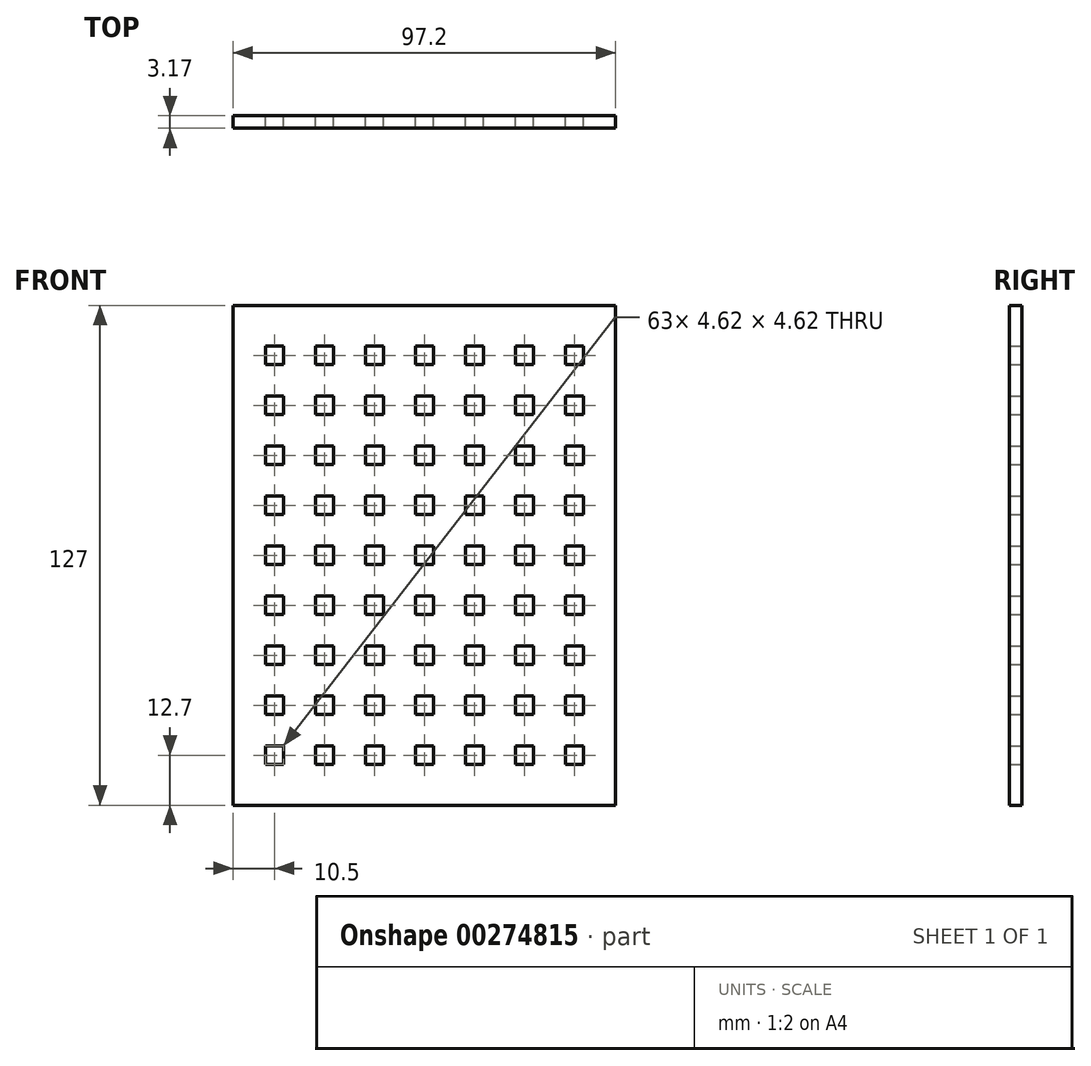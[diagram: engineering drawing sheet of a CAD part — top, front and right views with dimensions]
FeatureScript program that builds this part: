
annotation { "Feature Type Name" : "Feature", "Feature Type Description" : "" }
export const myFeature = defineFeature(function(context is Context, id is Id, definition is map)
    precondition{}
    {
        {
            var Q0;
            Q0=qCreatedBy(makeId("Front.planeOp"),FACE);
            var sketch = newSketch(context, id + "F0", { "sketchPlane" : qUnion([Q0])});
            skLineSegment(sketch, "E0.bottom", {"start": v(48.6, 63.5) * mm, "end": v(-48.6, 63.5) * mm});
            skLineSegment(sketch, "E0.top", {"start": v(48.6, -63.5) * mm, "end": v(-48.6, -63.5) * mm});
            skLineSegment(sketch, "E0.left", {"start": v(48.6, 63.5) * mm, "end": v(48.6, -63.5) * mm});
            skLineSegment(sketch, "E0.right", {"start": v(-48.6, 63.5) * mm, "end": v(-48.6, -63.5) * mm});
            skPoint(sketch, "E0.middle", {"position": v(0, 0) * mm});
            skLineSegment(sketch, "E1.bottom", {"start": v(2.31, 2.31) * mm, "end": v(-2.31, 2.31) * mm});
            skLineSegment(sketch, "E1.top", {"start": v(2.31, -2.31) * mm, "end": v(-2.31, -2.31) * mm});
            skLineSegment(sketch, "E1.left", {"start": v(2.31, 2.31) * mm, "end": v(2.31, -2.31) * mm});
            skLineSegment(sketch, "E1.right", {"start": v(-2.31, 2.31) * mm, "end": v(-2.31, -2.31) * mm});
            skLineSegment(sketch, "E2.0.1.0", {"start": v(2.31, -10.39) * mm, "end": v(-2.31, -10.39) * mm});
            skLineSegment(sketch, "E2.0.1.1", {"start": v(2.31, -15.01) * mm, "end": v(-2.31, -15.01) * mm});
            skLineSegment(sketch, "E2.0.1.2", {"start": v(2.31, -10.39) * mm, "end": v(2.31, -15.01) * mm});
            skPoint(sketch, "E2.0.1.3", {"position": v(0, -12.7) * mm});
            skLineSegment(sketch, "E2.0.1.4", {"start": v(-2.31, -10.39) * mm, "end": v(-2.31, -15.01) * mm});
            skPoint(sketch, "E2.0.1.5", {"position": v(0, -12.7) * mm});
            skLineSegment(sketch, "E2.0.2.0", {"start": v(2.31, -23.09) * mm, "end": v(-2.31, -23.09) * mm});
            skLineSegment(sketch, "E2.0.2.1", {"start": v(2.31, -27.71) * mm, "end": v(-2.31, -27.71) * mm});
            skLineSegment(sketch, "E2.0.2.2", {"start": v(2.31, -23.09) * mm, "end": v(2.31, -27.71) * mm});
            skPoint(sketch, "E2.0.2.3", {"position": v(0, -25.4) * mm});
            skLineSegment(sketch, "E2.0.2.4", {"start": v(-2.31, -23.09) * mm, "end": v(-2.31, -27.71) * mm});
            skPoint(sketch, "E2.0.2.5", {"position": v(0, -25.4) * mm});
            skLineSegment(sketch, "E2.0.3.0", {"start": v(2.31, -35.79) * mm, "end": v(-2.31, -35.79) * mm});
            skLineSegment(sketch, "E2.0.3.1", {"start": v(2.31, -40.41) * mm, "end": v(-2.31, -40.41) * mm});
            skLineSegment(sketch, "E2.0.3.2", {"start": v(2.31, -35.79) * mm, "end": v(2.31, -40.41) * mm});
            skPoint(sketch, "E2.0.3.3", {"position": v(0, -38.1) * mm});
            skLineSegment(sketch, "E2.0.3.4", {"start": v(-2.31, -35.79) * mm, "end": v(-2.31, -40.41) * mm});
            skPoint(sketch, "E2.0.3.5", {"position": v(0, -38.1) * mm});
            skLineSegment(sketch, "E2.0.4.0", {"start": v(2.31, -48.49) * mm, "end": v(-2.31, -48.49) * mm});
            skLineSegment(sketch, "E2.0.4.1", {"start": v(2.31, -53.11) * mm, "end": v(-2.31, -53.11) * mm});
            skLineSegment(sketch, "E2.0.4.2", {"start": v(2.31, -48.49) * mm, "end": v(2.31, -53.11) * mm});
            skPoint(sketch, "E2.0.4.3", {"position": v(0, -50.8) * mm});
            skLineSegment(sketch, "E2.0.4.4", {"start": v(-2.31, -48.49) * mm, "end": v(-2.31, -53.11) * mm});
            skPoint(sketch, "E2.0.4.5", {"position": v(0, -50.8) * mm});
            skLineSegment(sketch, "E2.1.0.0", {"start": v(15.01, 2.31) * mm, "end": v(10.39, 2.31) * mm});
            skLineSegment(sketch, "E2.1.0.1", {"start": v(15.01, -2.31) * mm, "end": v(10.39, -2.31) * mm});
            skLineSegment(sketch, "E2.1.0.2", {"start": v(15.01, 2.31) * mm, "end": v(15.01, -2.31) * mm});
            skPoint(sketch, "E2.1.0.3", {"position": v(12.7, 0) * mm});
            skLineSegment(sketch, "E2.1.0.4", {"start": v(10.39, 2.31) * mm, "end": v(10.39, -2.31) * mm});
            skPoint(sketch, "E2.1.0.5", {"position": v(12.7, 0) * mm});
            skLineSegment(sketch, "E2.1.1.0", {"start": v(15.01, -10.39) * mm, "end": v(10.39, -10.39) * mm});
            skLineSegment(sketch, "E2.1.1.1", {"start": v(15.01, -15.01) * mm, "end": v(10.39, -15.01) * mm});
            skLineSegment(sketch, "E2.1.1.2", {"start": v(15.01, -10.39) * mm, "end": v(15.01, -15.01) * mm});
            skPoint(sketch, "E2.1.1.3", {"position": v(12.7, -12.7) * mm});
            skLineSegment(sketch, "E2.1.1.4", {"start": v(10.39, -10.39) * mm, "end": v(10.39, -15.01) * mm});
            skPoint(sketch, "E2.1.1.5", {"position": v(12.7, -12.7) * mm});
            skLineSegment(sketch, "E2.1.2.0", {"start": v(15.01, -23.09) * mm, "end": v(10.39, -23.09) * mm});
            skLineSegment(sketch, "E2.1.2.1", {"start": v(15.01, -27.71) * mm, "end": v(10.39, -27.71) * mm});
            skLineSegment(sketch, "E2.1.2.2", {"start": v(15.01, -23.09) * mm, "end": v(15.01, -27.71) * mm});
            skPoint(sketch, "E2.1.2.3", {"position": v(12.7, -25.4) * mm});
            skLineSegment(sketch, "E2.1.2.4", {"start": v(10.39, -23.09) * mm, "end": v(10.39, -27.71) * mm});
            skPoint(sketch, "E2.1.2.5", {"position": v(12.7, -25.4) * mm});
            skLineSegment(sketch, "E2.1.3.0", {"start": v(15.01, -35.79) * mm, "end": v(10.39, -35.79) * mm});
            skLineSegment(sketch, "E2.1.3.1", {"start": v(15.01, -40.41) * mm, "end": v(10.39, -40.41) * mm});
            skLineSegment(sketch, "E2.1.3.2", {"start": v(15.01, -35.79) * mm, "end": v(15.01, -40.41) * mm});
            skPoint(sketch, "E2.1.3.3", {"position": v(12.7, -38.1) * mm});
            skLineSegment(sketch, "E2.1.3.4", {"start": v(10.39, -35.79) * mm, "end": v(10.39, -40.41) * mm});
            skPoint(sketch, "E2.1.3.5", {"position": v(12.7, -38.1) * mm});
            skLineSegment(sketch, "E2.1.4.0", {"start": v(15.01, -48.49) * mm, "end": v(10.39, -48.49) * mm});
            skLineSegment(sketch, "E2.1.4.1", {"start": v(15.01, -53.11) * mm, "end": v(10.39, -53.11) * mm});
            skLineSegment(sketch, "E2.1.4.2", {"start": v(15.01, -48.49) * mm, "end": v(15.01, -53.11) * mm});
            skPoint(sketch, "E2.1.4.3", {"position": v(12.7, -50.8) * mm});
            skLineSegment(sketch, "E2.1.4.4", {"start": v(10.39, -48.49) * mm, "end": v(10.39, -53.11) * mm});
            skPoint(sketch, "E2.1.4.5", {"position": v(12.7, -50.8) * mm});
            skLineSegment(sketch, "E2.2.0.0", {"start": v(27.71, 2.31) * mm, "end": v(23.09, 2.31) * mm});
            skLineSegment(sketch, "E2.2.0.1", {"start": v(27.71, -2.31) * mm, "end": v(23.09, -2.31) * mm});
            skLineSegment(sketch, "E2.2.0.2", {"start": v(27.71, 2.31) * mm, "end": v(27.71, -2.31) * mm});
            skPoint(sketch, "E2.2.0.3", {"position": v(25.4, 0) * mm});
            skLineSegment(sketch, "E2.2.0.4", {"start": v(23.09, 2.31) * mm, "end": v(23.09, -2.31) * mm});
            skPoint(sketch, "E2.2.0.5", {"position": v(25.4, 0) * mm});
            skLineSegment(sketch, "E2.2.1.0", {"start": v(27.71, -10.39) * mm, "end": v(23.09, -10.39) * mm});
            skLineSegment(sketch, "E2.2.1.1", {"start": v(27.71, -15.01) * mm, "end": v(23.09, -15.01) * mm});
            skLineSegment(sketch, "E2.2.1.2", {"start": v(27.71, -10.39) * mm, "end": v(27.71, -15.01) * mm});
            skPoint(sketch, "E2.2.1.3", {"position": v(25.4, -12.7) * mm});
            skLineSegment(sketch, "E2.2.1.4", {"start": v(23.09, -10.39) * mm, "end": v(23.09, -15.01) * mm});
            skPoint(sketch, "E2.2.1.5", {"position": v(25.4, -12.7) * mm});
            skLineSegment(sketch, "E2.2.2.0", {"start": v(27.71, -23.09) * mm, "end": v(23.09, -23.09) * mm});
            skLineSegment(sketch, "E2.2.2.1", {"start": v(27.71, -27.71) * mm, "end": v(23.09, -27.71) * mm});
            skLineSegment(sketch, "E2.2.2.2", {"start": v(27.71, -23.09) * mm, "end": v(27.71, -27.71) * mm});
            skPoint(sketch, "E2.2.2.3", {"position": v(25.4, -25.4) * mm});
            skLineSegment(sketch, "E2.2.2.4", {"start": v(23.09, -23.09) * mm, "end": v(23.09, -27.71) * mm});
            skPoint(sketch, "E2.2.2.5", {"position": v(25.4, -25.4) * mm});
            skLineSegment(sketch, "E2.2.3.0", {"start": v(27.71, -35.79) * mm, "end": v(23.09, -35.79) * mm});
            skLineSegment(sketch, "E2.2.3.1", {"start": v(27.71, -40.41) * mm, "end": v(23.09, -40.41) * mm});
            skLineSegment(sketch, "E2.2.3.2", {"start": v(27.71, -35.79) * mm, "end": v(27.71, -40.41) * mm});
            skPoint(sketch, "E2.2.3.3", {"position": v(25.4, -38.1) * mm});
            skLineSegment(sketch, "E2.2.3.4", {"start": v(23.09, -35.79) * mm, "end": v(23.09, -40.41) * mm});
            skPoint(sketch, "E2.2.3.5", {"position": v(25.4, -38.1) * mm});
            skLineSegment(sketch, "E2.2.4.0", {"start": v(27.71, -48.49) * mm, "end": v(23.09, -48.49) * mm});
            skLineSegment(sketch, "E2.2.4.1", {"start": v(27.71, -53.11) * mm, "end": v(23.09, -53.11) * mm});
            skLineSegment(sketch, "E2.2.4.2", {"start": v(27.71, -48.49) * mm, "end": v(27.71, -53.11) * mm});
            skPoint(sketch, "E2.2.4.3", {"position": v(25.4, -50.8) * mm});
            skLineSegment(sketch, "E2.2.4.4", {"start": v(23.09, -48.49) * mm, "end": v(23.09, -53.11) * mm});
            skPoint(sketch, "E2.2.4.5", {"position": v(25.4, -50.8) * mm});
            skLineSegment(sketch, "E2.3.0.0", {"start": v(40.41, 2.31) * mm, "end": v(35.79, 2.31) * mm});
            skLineSegment(sketch, "E2.3.0.1", {"start": v(40.41, -2.31) * mm, "end": v(35.79, -2.31) * mm});
            skLineSegment(sketch, "E2.3.0.2", {"start": v(40.41, 2.31) * mm, "end": v(40.41, -2.31) * mm});
            skPoint(sketch, "E2.3.0.3", {"position": v(38.1, 0) * mm});
            skLineSegment(sketch, "E2.3.0.4", {"start": v(35.79, 2.31) * mm, "end": v(35.79, -2.31) * mm});
            skPoint(sketch, "E2.3.0.5", {"position": v(38.1, 0) * mm});
            skLineSegment(sketch, "E2.3.1.0", {"start": v(40.41, -10.39) * mm, "end": v(35.79, -10.39) * mm});
            skLineSegment(sketch, "E2.3.1.1", {"start": v(40.41, -15.01) * mm, "end": v(35.79, -15.01) * mm});
            skLineSegment(sketch, "E2.3.1.2", {"start": v(40.41, -10.39) * mm, "end": v(40.41, -15.01) * mm});
            skPoint(sketch, "E2.3.1.3", {"position": v(38.1, -12.7) * mm});
            skLineSegment(sketch, "E2.3.1.4", {"start": v(35.79, -10.39) * mm, "end": v(35.79, -15.01) * mm});
            skPoint(sketch, "E2.3.1.5", {"position": v(38.1, -12.7) * mm});
            skLineSegment(sketch, "E2.3.2.0", {"start": v(40.41, -23.09) * mm, "end": v(35.79, -23.09) * mm});
            skLineSegment(sketch, "E2.3.2.1", {"start": v(40.41, -27.71) * mm, "end": v(35.79, -27.71) * mm});
            skLineSegment(sketch, "E2.3.2.2", {"start": v(40.41, -23.09) * mm, "end": v(40.41, -27.71) * mm});
            skPoint(sketch, "E2.3.2.3", {"position": v(38.1, -25.4) * mm});
            skLineSegment(sketch, "E2.3.2.4", {"start": v(35.79, -23.09) * mm, "end": v(35.79, -27.71) * mm});
            skPoint(sketch, "E2.3.2.5", {"position": v(38.1, -25.4) * mm});
            skLineSegment(sketch, "E2.3.3.0", {"start": v(40.41, -35.79) * mm, "end": v(35.79, -35.79) * mm});
            skLineSegment(sketch, "E2.3.3.1", {"start": v(40.41, -40.41) * mm, "end": v(35.79, -40.41) * mm});
            skLineSegment(sketch, "E2.3.3.2", {"start": v(40.41, -35.79) * mm, "end": v(40.41, -40.41) * mm});
            skPoint(sketch, "E2.3.3.3", {"position": v(38.1, -38.1) * mm});
            skLineSegment(sketch, "E2.3.3.4", {"start": v(35.79, -35.79) * mm, "end": v(35.79, -40.41) * mm});
            skPoint(sketch, "E2.3.3.5", {"position": v(38.1, -38.1) * mm});
            skLineSegment(sketch, "E2.3.4.0", {"start": v(40.41, -48.49) * mm, "end": v(35.79, -48.49) * mm});
            skLineSegment(sketch, "E2.3.4.1", {"start": v(40.41, -53.11) * mm, "end": v(35.79, -53.11) * mm});
            skLineSegment(sketch, "E2.3.4.2", {"start": v(40.41, -48.49) * mm, "end": v(40.41, -53.11) * mm});
            skPoint(sketch, "E2.3.4.3", {"position": v(38.1, -50.8) * mm});
            skLineSegment(sketch, "E2.3.4.4", {"start": v(35.79, -48.49) * mm, "end": v(35.79, -53.11) * mm});
            skPoint(sketch, "E2.3.4.5", {"position": v(38.1, -50.8) * mm});
            skLineSegment(sketch, "E3.MirrorCS", {"start": v(23.09, 10.39) * mm, "end": v(23.09, 15.01) * mm});
            skLineSegment(sketch, "E4.MirrorCS", {"start": v(23.09, 35.79) * mm, "end": v(23.09, 40.41) * mm});
            skLineSegment(sketch, "E5.MirrorCS", {"start": v(27.71, 53.11) * mm, "end": v(23.09, 53.11) * mm});
            skLineSegment(sketch, "E6.MirrorCS", {"start": v(2.31, 53.11) * mm, "end": v(-2.31, 53.11) * mm});
            skLineSegment(sketch, "E7.MirrorCS", {"start": v(27.71, 27.71) * mm, "end": v(23.09, 27.71) * mm});
            skLineSegment(sketch, "E8.MirrorCS", {"start": v(23.09, 48.49) * mm, "end": v(23.09, 53.11) * mm});
            skLineSegment(sketch, "E9.MirrorCS", {"start": v(23.09, -2.31) * mm, "end": v(23.09, 2.31) * mm});
            skLineSegment(sketch, "E10.MirrorCS", {"start": v(2.31, 27.71) * mm, "end": v(-2.31, 27.71) * mm});
            skLineSegment(sketch, "E11.MirrorCS", {"start": v(23.09, 23.09) * mm, "end": v(23.09, 27.71) * mm});
            skLineSegment(sketch, "E12.MirrorCS", {"start": v(40.41, 53.11) * mm, "end": v(35.79, 53.11) * mm});
            skLineSegment(sketch, "E13.MirrorCS", {"start": v(15.01, 27.71) * mm, "end": v(10.39, 27.71) * mm});
            skLineSegment(sketch, "E14.MirrorCS", {"start": v(40.41, 27.71) * mm, "end": v(35.79, 27.71) * mm});
            skLineSegment(sketch, "E15.MirrorCS", {"start": v(15.01, 53.11) * mm, "end": v(10.39, 53.11) * mm});
            skPoint(sketch, "E16.MirrorP", {"position": v(0, 25.4) * mm});
            skPoint(sketch, "E17.MirrorP", {"position": v(38.1, 38.1) * mm});
            skPoint(sketch, "E18.MirrorP", {"position": v(25.4, 50.8) * mm});
            skPoint(sketch, "E19.MirrorP", {"position": v(12.7, 12.7) * mm});
            skPoint(sketch, "E20.MirrorP", {"position": v(12.7, 25.4) * mm});
            skPoint(sketch, "E21.MirrorP", {"position": v(25.4, 12.7) * mm});
            skPoint(sketch, "E22.MirrorP", {"position": v(0, 38.1) * mm});
            skPoint(sketch, "E23.MirrorP", {"position": v(38.1, 50.8) * mm});
            skPoint(sketch, "E24.MirrorP", {"position": v(12.7, 38.1) * mm});
            skPoint(sketch, "E25.MirrorP", {"position": v(38.1, 12.7) * mm});
            skLineSegment(sketch, "E26.MirrorCS", {"start": v(15.01, 10.39) * mm, "end": v(10.39, 10.39) * mm});
            skPoint(sketch, "E27.MirrorP", {"position": v(25.4, 25.4) * mm});
            skPoint(sketch, "E28.MirrorP", {"position": v(0, 50.8) * mm});
            skLineSegment(sketch, "E29.MirrorCS", {"start": v(-2.31, 10.39) * mm, "end": v(-2.31, 15.01) * mm});
            skPoint(sketch, "E30.MirrorP", {"position": v(12.7, 50.8) * mm});
            skPoint(sketch, "E31.MirrorP", {"position": v(0, 12.7) * mm});
            skPoint(sketch, "E32.MirrorP", {"position": v(38.1, 25.4) * mm});
            skPoint(sketch, "E33.MirrorP", {"position": v(25.4, 38.1) * mm});
            skLineSegment(sketch, "E34.MirrorCS", {"start": v(15.01, 23.09) * mm, "end": v(15.01, 27.71) * mm});
            skLineSegment(sketch, "E35.MirrorCS", {"start": v(27.71, 10.39) * mm, "end": v(27.71, 15.01) * mm});
            skLineSegment(sketch, "E36.MirrorCS", {"start": v(27.71, 35.79) * mm, "end": v(27.71, 40.41) * mm});
            skLineSegment(sketch, "E37.MirrorCS", {"start": v(15.01, 48.49) * mm, "end": v(15.01, 53.11) * mm});
            skLineSegment(sketch, "E38.MirrorCS", {"start": v(15.01, -2.31) * mm, "end": v(15.01, 2.31) * mm});
            skLineSegment(sketch, "E39.MirrorCS", {"start": v(40.41, 23.09) * mm, "end": v(40.41, 27.71) * mm});
            skLineSegment(sketch, "E40.MirrorCS", {"start": v(-2.31, 35.79) * mm, "end": v(-2.31, 40.41) * mm});
            skLineSegment(sketch, "E41.MirrorCS", {"start": v(35.79, 48.49) * mm, "end": v(35.79, 53.11) * mm});
            skLineSegment(sketch, "E42.MirrorCS", {"start": v(35.79, -2.31) * mm, "end": v(35.79, 2.31) * mm});
            skLineSegment(sketch, "E43.MirrorCS", {"start": v(10.39, 23.09) * mm, "end": v(10.39, 27.71) * mm});
            skLineSegment(sketch, "E44.MirrorCS", {"start": v(10.39, 48.49) * mm, "end": v(10.39, 53.11) * mm});
            skLineSegment(sketch, "E45.MirrorCS", {"start": v(10.39, -2.31) * mm, "end": v(10.39, 2.31) * mm});
            skLineSegment(sketch, "E46.MirrorCS", {"start": v(35.79, 23.09) * mm, "end": v(35.79, 27.71) * mm});
            skLineSegment(sketch, "E47.MirrorCS", {"start": v(2.31, 48.49) * mm, "end": v(-2.31, 48.49) * mm});
            skLineSegment(sketch, "E48.MirrorCS", {"start": v(40.41, 40.41) * mm, "end": v(35.79, 40.41) * mm});
            skLineSegment(sketch, "E49.MirrorCS", {"start": v(40.41, 10.39) * mm, "end": v(35.79, 10.39) * mm});
            skLineSegment(sketch, "E50.MirrorCS", {"start": v(27.71, 23.09) * mm, "end": v(23.09, 23.09) * mm});
            skLineSegment(sketch, "E51.MirrorCS", {"start": v(15.01, 35.79) * mm, "end": v(10.39, 35.79) * mm});
            skLineSegment(sketch, "E52.MirrorCS", {"start": v(15.01, 15.01) * mm, "end": v(10.39, 15.01) * mm});
            skLineSegment(sketch, "E53.MirrorCS", {"start": v(27.71, 48.49) * mm, "end": v(23.09, 48.49) * mm});
            skLineSegment(sketch, "E54.MirrorCS", {"start": v(40.41, 35.79) * mm, "end": v(35.79, 35.79) * mm});
            skLineSegment(sketch, "E55.MirrorCS", {"start": v(40.41, 35.79) * mm, "end": v(40.41, 40.41) * mm});
            skLineSegment(sketch, "E56.MirrorCS", {"start": v(27.71, 48.49) * mm, "end": v(27.71, 53.11) * mm});
            skLineSegment(sketch, "E57.MirrorCS", {"start": v(40.41, 15.01) * mm, "end": v(35.79, 15.01) * mm});
            skLineSegment(sketch, "E58.MirrorCS", {"start": v(27.71, -2.31) * mm, "end": v(27.71, 2.31) * mm});
            skLineSegment(sketch, "E59.MirrorCS", {"start": v(15.01, 40.41) * mm, "end": v(10.39, 40.41) * mm});
            skLineSegment(sketch, "E60.MirrorCS", {"start": v(15.01, 10.39) * mm, "end": v(15.01, 15.01) * mm});
            skLineSegment(sketch, "E61.MirrorCS", {"start": v(2.31, 48.49) * mm, "end": v(2.31, 53.11) * mm});
            skLineSegment(sketch, "E62.MirrorCS", {"start": v(35.79, 35.79) * mm, "end": v(35.79, 40.41) * mm});
            skLineSegment(sketch, "E63.MirrorCS", {"start": v(40.41, 10.39) * mm, "end": v(40.41, 15.01) * mm});
            skLineSegment(sketch, "E64.MirrorCS", {"start": v(27.71, 23.09) * mm, "end": v(27.71, 27.71) * mm});
            skLineSegment(sketch, "E65.MirrorCS", {"start": v(15.01, 35.79) * mm, "end": v(15.01, 40.41) * mm});
            skLineSegment(sketch, "E66.MirrorCS", {"start": v(10.39, 10.39) * mm, "end": v(10.39, 15.01) * mm});
            skLineSegment(sketch, "E67.MirrorCS", {"start": v(2.31, 23.09) * mm, "end": v(2.31, 27.71) * mm});
            skLineSegment(sketch, "E68.MirrorCS", {"start": v(-2.31, 23.09) * mm, "end": v(-2.31, 27.71) * mm});
            skLineSegment(sketch, "E69.MirrorCS", {"start": v(2.31, -2.31) * mm, "end": v(2.31, 2.31) * mm});
            skLineSegment(sketch, "E70.MirrorCS", {"start": v(-2.31, -2.31) * mm, "end": v(-2.31, 2.31) * mm});
            skLineSegment(sketch, "E71.MirrorCS", {"start": v(2.31, 10.39) * mm, "end": v(-2.31, 10.39) * mm});
            skLineSegment(sketch, "E72.MirrorCS", {"start": v(2.31, 15.01) * mm, "end": v(-2.31, 15.01) * mm});
            skLineSegment(sketch, "E73.MirrorCS", {"start": v(2.31, 10.39) * mm, "end": v(2.31, 15.01) * mm});
            skLineSegment(sketch, "E74.MirrorCS", {"start": v(2.31, 23.09) * mm, "end": v(-2.31, 23.09) * mm});
            skLineSegment(sketch, "E75.MirrorCS", {"start": v(10.39, 35.79) * mm, "end": v(10.39, 40.41) * mm});
            skLineSegment(sketch, "E76.MirrorCS", {"start": v(-2.31, 48.49) * mm, "end": v(-2.31, 53.11) * mm});
            skLineSegment(sketch, "E77.MirrorCS", {"start": v(35.79, 10.39) * mm, "end": v(35.79, 15.01) * mm});
            skLineSegment(sketch, "E78.MirrorCS", {"start": v(2.31, 35.79) * mm, "end": v(-2.31, 35.79) * mm});
            skLineSegment(sketch, "E79.MirrorCS", {"start": v(40.41, 48.49) * mm, "end": v(35.79, 48.49) * mm});
            skLineSegment(sketch, "E80.MirrorCS", {"start": v(27.71, 10.39) * mm, "end": v(23.09, 10.39) * mm});
            skLineSegment(sketch, "E81.MirrorCS", {"start": v(15.01, 23.09) * mm, "end": v(10.39, 23.09) * mm});
            skLineSegment(sketch, "E82.MirrorCS", {"start": v(27.71, 35.79) * mm, "end": v(23.09, 35.79) * mm});
            skLineSegment(sketch, "E83.MirrorCS", {"start": v(15.01, 48.49) * mm, "end": v(10.39, 48.49) * mm});
            skLineSegment(sketch, "E84.MirrorCS", {"start": v(40.41, 23.09) * mm, "end": v(35.79, 23.09) * mm});
            skLineSegment(sketch, "E85.MirrorCS", {"start": v(2.31, 40.41) * mm, "end": v(-2.31, 40.41) * mm});
            skLineSegment(sketch, "E86.MirrorCS", {"start": v(27.71, 15.01) * mm, "end": v(23.09, 15.01) * mm});
            skLineSegment(sketch, "E87.MirrorCS", {"start": v(40.41, -2.31) * mm, "end": v(40.41, 2.31) * mm});
            skLineSegment(sketch, "E88.MirrorCS", {"start": v(40.41, 48.49) * mm, "end": v(40.41, 53.11) * mm});
            skLineSegment(sketch, "E89.MirrorCS", {"start": v(2.31, 35.79) * mm, "end": v(2.31, 40.41) * mm});
            skLineSegment(sketch, "E90.MirrorCS", {"start": v(27.71, 40.41) * mm, "end": v(23.09, 40.41) * mm});
            skPoint(sketch, "E91.endSnap0", {"position": v(0, 2.31) * mm});
            skLineSegment(sketch, "E92.MirrorCS", {"start": v(-40.41, -2.31) * mm, "end": v(-35.79, -2.31) * mm});
            skLineSegment(sketch, "E93.MirrorCS", {"start": v(-2.31, -2.31) * mm, "end": v(2.31, -2.31) * mm});
            skLineSegment(sketch, "E94.MirrorCS", {"start": v(-23.09, -2.31) * mm, "end": v(-23.09, 2.31) * mm});
            skLineSegment(sketch, "E95.MirrorCS", {"start": v(-15.01, 2.31) * mm, "end": v(-15.01, -2.31) * mm});
            skLineSegment(sketch, "E96.MirrorCS", {"start": v(-27.71, -2.31) * mm, "end": v(-23.09, -2.31) * mm});
            skLineSegment(sketch, "E97.MirrorCS", {"start": v(-15.01, -2.31) * mm, "end": v(-10.39, -2.31) * mm});
            skLineSegment(sketch, "E98.MirrorCS", {"start": v(-23.09, 2.31) * mm, "end": v(-23.09, -2.31) * mm});
            skLineSegment(sketch, "E99.MirrorCS", {"start": v(-15.01, -2.31) * mm, "end": v(-15.01, 2.31) * mm});
            skPoint(sketch, "E100.MirrorP", {"position": v(-25.4, 0) * mm});
            skPoint(sketch, "E101.MirrorP", {"position": v(-38.1, 0) * mm});
            skLineSegment(sketch, "E102.MirrorCS", {"start": v(-15.01, -27.71) * mm, "end": v(-10.39, -27.71) * mm});
            skLineSegment(sketch, "E103.MirrorCS", {"start": v(-40.41, -53.11) * mm, "end": v(-35.79, -53.11) * mm});
            skLineSegment(sketch, "E104.MirrorCS", {"start": v(-15.01, -23.09) * mm, "end": v(-15.01, -27.71) * mm});
            skLineSegment(sketch, "E105.MirrorCS", {"start": v(-23.09, 23.09) * mm, "end": v(-23.09, 27.71) * mm});
            skLineSegment(sketch, "E106.MirrorCS", {"start": v(-2.31, -27.71) * mm, "end": v(2.31, -27.71) * mm});
            skLineSegment(sketch, "E107.MirrorCS", {"start": v(-23.09, -48.49) * mm, "end": v(-23.09, -53.11) * mm});
            skLineSegment(sketch, "E108.MirrorCS", {"start": v(-2.31, 27.71) * mm, "end": v(2.31, 27.71) * mm});
            skLineSegment(sketch, "E109.MirrorCS", {"start": v(-15.01, -10.39) * mm, "end": v(-15.01, -15.01) * mm});
            skLineSegment(sketch, "E110.MirrorCS", {"start": v(-15.01, 35.79) * mm, "end": v(-15.01, 40.41) * mm});
            skLineSegment(sketch, "E111.MirrorCS", {"start": v(-23.09, 48.49) * mm, "end": v(-23.09, 53.11) * mm});
            skLineSegment(sketch, "E112.MirrorCS", {"start": v(-15.01, 48.49) * mm, "end": v(-15.01, 53.11) * mm});
            skLineSegment(sketch, "E113.MirrorCS", {"start": v(-27.71, -53.11) * mm, "end": v(-23.09, -53.11) * mm});
            skLineSegment(sketch, "E114.MirrorCS", {"start": v(-27.71, 27.71) * mm, "end": v(-23.09, 27.71) * mm});
            skLineSegment(sketch, "E115.MirrorCS", {"start": v(-23.09, -35.79) * mm, "end": v(-23.09, -40.41) * mm});
            skLineSegment(sketch, "E116.MirrorCS", {"start": v(-15.01, 10.39) * mm, "end": v(-15.01, 15.01) * mm});
            skLineSegment(sketch, "E117.MirrorCS", {"start": v(-23.09, 35.79) * mm, "end": v(-23.09, 40.41) * mm});
            skLineSegment(sketch, "E118.MirrorCS", {"start": v(-23.09, -23.09) * mm, "end": v(-23.09, -27.71) * mm});
            skLineSegment(sketch, "E119.MirrorCS", {"start": v(-15.01, 53.11) * mm, "end": v(-10.39, 53.11) * mm});
            skLineSegment(sketch, "E120.MirrorCS", {"start": v(-15.01, -35.79) * mm, "end": v(-15.01, -40.41) * mm});
            skLineSegment(sketch, "E121.MirrorCS", {"start": v(-23.09, 10.39) * mm, "end": v(-23.09, 15.01) * mm});
            skLineSegment(sketch, "E122.MirrorCS", {"start": v(-2.31, 53.11) * mm, "end": v(2.31, 53.11) * mm});
            skLineSegment(sketch, "E123.MirrorCS", {"start": v(-15.01, 23.09) * mm, "end": v(-15.01, 27.71) * mm});
            skLineSegment(sketch, "E124.MirrorCS", {"start": v(-15.01, -48.49) * mm, "end": v(-15.01, -53.11) * mm});
            skLineSegment(sketch, "E125.MirrorCS", {"start": v(-40.41, 27.71) * mm, "end": v(-35.79, 27.71) * mm});
            skLineSegment(sketch, "E126.MirrorCS", {"start": v(-27.71, -27.71) * mm, "end": v(-23.09, -27.71) * mm});
            skLineSegment(sketch, "E127.MirrorCS", {"start": v(-2.31, -53.11) * mm, "end": v(2.31, -53.11) * mm});
            skLineSegment(sketch, "E128.MirrorCS", {"start": v(-15.01, 27.71) * mm, "end": v(-10.39, 27.71) * mm});
            skLineSegment(sketch, "E129.MirrorCS", {"start": v(-40.41, -27.71) * mm, "end": v(-35.79, -27.71) * mm});
            skLineSegment(sketch, "E130.MirrorCS", {"start": v(-15.01, -53.11) * mm, "end": v(-10.39, -53.11) * mm});
            skLineSegment(sketch, "E131.MirrorCS", {"start": v(-40.41, 53.11) * mm, "end": v(-35.79, 53.11) * mm});
            skLineSegment(sketch, "E132.MirrorCS", {"start": v(-23.09, -10.39) * mm, "end": v(-23.09, -15.01) * mm});
            skLineSegment(sketch, "E133.MirrorCS", {"start": v(-2.31, 2.31) * mm, "end": v(2.31, 2.31) * mm});
            skLineSegment(sketch, "E134.MirrorCS", {"start": v(-27.71, 53.11) * mm, "end": v(-23.09, 53.11) * mm});
            skLineSegment(sketch, "E135.MirrorCS", {"start": v(-40.41, 2.31) * mm, "end": v(-35.79, 2.31) * mm});
            skPoint(sketch, "E136.MirrorP", {"position": v(-12.7, -25.4) * mm});
            skPoint(sketch, "E137.MirrorP", {"position": v(-25.4, 12.7) * mm});
            skPoint(sketch, "E138.MirrorP", {"position": v(-38.1, 38.1) * mm});
            skPoint(sketch, "E139.MirrorP", {"position": v(-25.4, 38.1) * mm});
            skLineSegment(sketch, "E140.MirrorCS", {"start": v(-15.01, -10.39) * mm, "end": v(-10.39, -10.39) * mm});
            skLineSegment(sketch, "E141.MirrorCS", {"start": v(-27.71, 2.31) * mm, "end": v(-23.09, 2.31) * mm});
            skPoint(sketch, "E142.MirrorP", {"position": v(-12.7, -12.7) * mm});
            skPoint(sketch, "E143.MirrorP", {"position": v(-25.4, -50.8) * mm});
            skPoint(sketch, "E144.MirrorP", {"position": v(-12.7, 12.7) * mm});
            skPoint(sketch, "E145.MirrorP", {"position": v(-25.4, -38.1) * mm});
            skPoint(sketch, "E146.MirrorP", {"position": v(-25.4, 50.8) * mm});
            skPoint(sketch, "E147.MirrorP", {"position": v(-38.1, 25.4) * mm});
            skPoint(sketch, "E148.MirrorP", {"position": v(-25.4, -12.7) * mm});
            skPoint(sketch, "E149.MirrorP", {"position": v(-25.4, 25.4) * mm});
            skLineSegment(sketch, "E150.MirrorCS", {"start": v(-15.01, 2.31) * mm, "end": v(-10.39, 2.31) * mm});
            skPoint(sketch, "E151.MirrorP", {"position": v(-12.7, 25.4) * mm});
            skPoint(sketch, "E152.MirrorP", {"position": v(-38.1, -38.1) * mm});
            skPoint(sketch, "E153.MirrorP", {"position": v(-38.1, 12.7) * mm});
            skPoint(sketch, "E154.MirrorP", {"position": v(-25.4, -25.4) * mm});
            skLineSegment(sketch, "E155.MirrorCS", {"start": v(-10.39, -2.31) * mm, "end": v(-10.39, 2.31) * mm});
            skLineSegment(sketch, "E156.MirrorCS", {"start": v(-27.71, -2.31) * mm, "end": v(-27.71, 2.31) * mm});
            skPoint(sketch, "E157.MirrorP", {"position": v(-38.1, -50.8) * mm});
            skPoint(sketch, "E158.MirrorP", {"position": v(-38.1, 50.8) * mm});
            skPoint(sketch, "E159.MirrorP", {"position": v(-38.1, -25.4) * mm});
            skPoint(sketch, "E160.MirrorP", {"position": v(-12.7, -50.8) * mm});
            skPoint(sketch, "E161.MirrorP", {"position": v(-12.7, 38.1) * mm});
            skPoint(sketch, "E162.MirrorP", {"position": v(-12.7, 50.8) * mm});
            skLineSegment(sketch, "E163.MirrorCS", {"start": v(-40.41, -2.31) * mm, "end": v(-40.41, 2.31) * mm});
            skLineSegment(sketch, "E164.MirrorCS", {"start": v(-35.79, 2.31) * mm, "end": v(-35.79, -2.31) * mm});
            skPoint(sketch, "E165.MirrorP", {"position": v(-12.7, -38.1) * mm});
            skPoint(sketch, "E166.MirrorP", {"position": v(-38.1, -12.7) * mm});
            skLineSegment(sketch, "E167.MirrorCS", {"start": v(-27.71, 15.01) * mm, "end": v(-23.09, 15.01) * mm});
            skLineSegment(sketch, "E168.MirrorCS", {"start": v(-40.41, 2.31) * mm, "end": v(-40.41, -2.31) * mm});
            skLineSegment(sketch, "E169.MirrorCS", {"start": v(-40.41, -48.49) * mm, "end": v(-40.41, -53.11) * mm});
            skLineSegment(sketch, "E170.MirrorCS", {"start": v(-35.79, 48.49) * mm, "end": v(-35.79, 53.11) * mm});
            skLineSegment(sketch, "E171.MirrorCS", {"start": v(-27.71, -15.01) * mm, "end": v(-23.09, -15.01) * mm});
            skLineSegment(sketch, "E172.MirrorCS", {"start": v(-2.31, -40.41) * mm, "end": v(2.31, -40.41) * mm});
            skLineSegment(sketch, "E173.MirrorCS", {"start": v(-2.31, 10.39) * mm, "end": v(2.31, 10.39) * mm});
            skLineSegment(sketch, "E174.MirrorCS", {"start": v(-15.01, -23.09) * mm, "end": v(-10.39, -23.09) * mm});
            skLineSegment(sketch, "E175.MirrorCS", {"start": v(-27.71, -10.39) * mm, "end": v(-23.09, -10.39) * mm});
            skLineSegment(sketch, "E176.MirrorCS", {"start": v(-40.41, -48.49) * mm, "end": v(-35.79, -48.49) * mm});
            skLineSegment(sketch, "E177.MirrorCS", {"start": v(-2.31, -35.79) * mm, "end": v(2.31, -35.79) * mm});
            skLineSegment(sketch, "E178.MirrorCS", {"start": v(-2.31, 40.41) * mm, "end": v(2.31, 40.41) * mm});
            skLineSegment(sketch, "E179.MirrorCS", {"start": v(-40.41, 35.79) * mm, "end": v(-35.79, 35.79) * mm});
            skLineSegment(sketch, "E180.MirrorCS", {"start": v(-2.31, -23.09) * mm, "end": v(2.31, -23.09) * mm});
            skLineSegment(sketch, "E181.MirrorCS", {"start": v(-2.31, -15.01) * mm, "end": v(2.31, -15.01) * mm});
            skLineSegment(sketch, "E182.MirrorCS", {"start": v(-2.31, -10.39) * mm, "end": v(2.31, -10.39) * mm});
            skLineSegment(sketch, "E183.MirrorCS", {"start": v(-40.41, 23.09) * mm, "end": v(-35.79, 23.09) * mm});
            skLineSegment(sketch, "E184.MirrorCS", {"start": v(-40.41, 23.09) * mm, "end": v(-40.41, 27.71) * mm});
            skLineSegment(sketch, "E185.MirrorCS", {"start": v(-27.71, 48.49) * mm, "end": v(-23.09, 48.49) * mm});
            skLineSegment(sketch, "E186.MirrorCS", {"start": v(-10.39, -10.39) * mm, "end": v(-10.39, -15.01) * mm});
            skLineSegment(sketch, "E187.MirrorCS", {"start": v(-35.79, -35.79) * mm, "end": v(-35.79, -40.41) * mm});
            skPoint(sketch, "E188.MirrorP", {"position": v(-12.7, 0) * mm});
            skLineSegment(sketch, "E189.MirrorCS", {"start": v(-15.01, 48.49) * mm, "end": v(-10.39, 48.49) * mm});
            skLineSegment(sketch, "E190.MirrorCS", {"start": v(-15.01, 15.01) * mm, "end": v(-10.39, 15.01) * mm});
            skLineSegment(sketch, "E191.MirrorCS", {"start": v(-27.71, 2.31) * mm, "end": v(-27.71, -2.31) * mm});
            skLineSegment(sketch, "E192.MirrorCS", {"start": v(-27.71, -48.49) * mm, "end": v(-27.71, -53.11) * mm});
            skLineSegment(sketch, "E193.MirrorCS", {"start": v(-40.41, -35.79) * mm, "end": v(-40.41, -40.41) * mm});
            skLineSegment(sketch, "E194.MirrorCS", {"start": v(-15.01, 23.09) * mm, "end": v(-10.39, 23.09) * mm});
            skLineSegment(sketch, "E195.MirrorCS", {"start": v(-40.41, -35.79) * mm, "end": v(-35.79, -35.79) * mm});
            skLineSegment(sketch, "E196.MirrorCS", {"start": v(-27.71, 35.79) * mm, "end": v(-27.71, 40.41) * mm});
            skLineSegment(sketch, "E197.MirrorCS", {"start": v(-27.71, -48.49) * mm, "end": v(-23.09, -48.49) * mm});
            skLineSegment(sketch, "E198.MirrorCS", {"start": v(-27.71, 35.79) * mm, "end": v(-23.09, 35.79) * mm});
            skLineSegment(sketch, "E199.MirrorCS", {"start": v(-15.01, 35.79) * mm, "end": v(-10.39, 35.79) * mm});
            skLineSegment(sketch, "E200.MirrorCS", {"start": v(-10.39, 10.39) * mm, "end": v(-10.39, 15.01) * mm});
            skLineSegment(sketch, "E201.MirrorCS", {"start": v(-15.01, -15.01) * mm, "end": v(-10.39, -15.01) * mm});
            skLineSegment(sketch, "E202.MirrorCS", {"start": v(-40.41, -40.41) * mm, "end": v(-35.79, -40.41) * mm});
            skLineSegment(sketch, "E203.MirrorCS", {"start": v(-27.71, 23.09) * mm, "end": v(-27.71, 27.71) * mm});
            skLineSegment(sketch, "E204.MirrorCS", {"start": v(-27.71, 10.39) * mm, "end": v(-23.09, 10.39) * mm});
            skLineSegment(sketch, "E205.MirrorCS", {"start": v(-35.79, -23.09) * mm, "end": v(-35.79, -27.71) * mm});
            skLineSegment(sketch, "E206.MirrorCS", {"start": v(-27.71, 10.39) * mm, "end": v(-27.71, 15.01) * mm});
            skLineSegment(sketch, "E207.MirrorCS", {"start": v(-27.71, 23.09) * mm, "end": v(-23.09, 23.09) * mm});
            skLineSegment(sketch, "E208.MirrorCS", {"start": v(-10.39, 2.31) * mm, "end": v(-10.39, -2.31) * mm});
            skLineSegment(sketch, "E209.MirrorCS", {"start": v(-35.79, -2.31) * mm, "end": v(-35.79, 2.31) * mm});
            skLineSegment(sketch, "E210.MirrorCS", {"start": v(-10.39, -48.49) * mm, "end": v(-10.39, -53.11) * mm});
            skLineSegment(sketch, "E211.MirrorCS", {"start": v(-27.71, 40.41) * mm, "end": v(-23.09, 40.41) * mm});
            skLineSegment(sketch, "E212.MirrorCS", {"start": v(-35.79, -10.39) * mm, "end": v(-35.79, -15.01) * mm});
            skLineSegment(sketch, "E213.MirrorCS", {"start": v(-15.01, 10.39) * mm, "end": v(-10.39, 10.39) * mm});
            skLineSegment(sketch, "E214.MirrorCS", {"start": v(-2.31, 48.49) * mm, "end": v(2.31, 48.49) * mm});
            skLineSegment(sketch, "E215.MirrorCS", {"start": v(-15.01, -48.49) * mm, "end": v(-10.39, -48.49) * mm});
            skLineSegment(sketch, "E216.MirrorCS", {"start": v(-10.39, -35.79) * mm, "end": v(-10.39, -40.41) * mm});
            skLineSegment(sketch, "E217.MirrorCS", {"start": v(-35.79, 23.09) * mm, "end": v(-35.79, 27.71) * mm});
            skLineSegment(sketch, "E218.MirrorCS", {"start": v(-15.01, 40.41) * mm, "end": v(-10.39, 40.41) * mm});
            skLineSegment(sketch, "E219.MirrorCS", {"start": v(-10.39, 35.79) * mm, "end": v(-10.39, 40.41) * mm});
            skLineSegment(sketch, "E220.MirrorCS", {"start": v(-27.71, -23.09) * mm, "end": v(-27.71, -27.71) * mm});
            skLineSegment(sketch, "E221.MirrorCS", {"start": v(-40.41, 10.39) * mm, "end": v(-40.41, 15.01) * mm});
            skLineSegment(sketch, "E222.MirrorCS", {"start": v(-40.41, -10.39) * mm, "end": v(-40.41, -15.01) * mm});
            skLineSegment(sketch, "E223.MirrorCS", {"start": v(-40.41, 48.49) * mm, "end": v(-35.79, 48.49) * mm});
            skLineSegment(sketch, "E224.MirrorCS", {"start": v(-27.71, -35.79) * mm, "end": v(-23.09, -35.79) * mm});
            skLineSegment(sketch, "E225.MirrorCS", {"start": v(-40.41, -23.09) * mm, "end": v(-40.41, -27.71) * mm});
            skLineSegment(sketch, "E226.MirrorCS", {"start": v(-40.41, 10.39) * mm, "end": v(-35.79, 10.39) * mm});
            skLineSegment(sketch, "E227.MirrorCS", {"start": v(-27.71, -35.79) * mm, "end": v(-27.71, -40.41) * mm});
            skLineSegment(sketch, "E228.MirrorCS", {"start": v(-2.31, 23.09) * mm, "end": v(2.31, 23.09) * mm});
            skLineSegment(sketch, "E229.MirrorCS", {"start": v(-15.01, -40.41) * mm, "end": v(-10.39, -40.41) * mm});
            skLineSegment(sketch, "E230.MirrorCS", {"start": v(-40.41, -15.01) * mm, "end": v(-35.79, -15.01) * mm});
            skLineSegment(sketch, "E231.MirrorCS", {"start": v(-40.41, 48.49) * mm, "end": v(-40.41, 53.11) * mm});
            skLineSegment(sketch, "E232.MirrorCS", {"start": v(-10.39, 48.49) * mm, "end": v(-10.39, 53.11) * mm});
            skLineSegment(sketch, "E233.MirrorCS", {"start": v(-40.41, 15.01) * mm, "end": v(-35.79, 15.01) * mm});
            skLineSegment(sketch, "E234.MirrorCS", {"start": v(-15.01, -35.79) * mm, "end": v(-10.39, -35.79) * mm});
            skLineSegment(sketch, "E235.MirrorCS", {"start": v(-27.71, -23.09) * mm, "end": v(-23.09, -23.09) * mm});
            skLineSegment(sketch, "E236.MirrorCS", {"start": v(-40.41, -10.39) * mm, "end": v(-35.79, -10.39) * mm});
            skLineSegment(sketch, "E237.MirrorCS", {"start": v(-2.31, -48.49) * mm, "end": v(2.31, -48.49) * mm});
            skLineSegment(sketch, "E238.MirrorCS", {"start": v(-35.79, 35.79) * mm, "end": v(-35.79, 40.41) * mm});
            skLineSegment(sketch, "E239.MirrorCS", {"start": v(-2.31, 35.79) * mm, "end": v(2.31, 35.79) * mm});
            skLineSegment(sketch, "E240.MirrorCS", {"start": v(-27.71, -40.41) * mm, "end": v(-23.09, -40.41) * mm});
            skLineSegment(sketch, "E241.MirrorCS", {"start": v(-10.39, 23.09) * mm, "end": v(-10.39, 27.71) * mm});
            skLineSegment(sketch, "E242.MirrorCS", {"start": v(-27.71, 48.49) * mm, "end": v(-27.71, 53.11) * mm});
            skLineSegment(sketch, "E243.MirrorCS", {"start": v(-2.31, 15.01) * mm, "end": v(2.31, 15.01) * mm});
            skLineSegment(sketch, "E244.MirrorCS", {"start": v(-10.39, -23.09) * mm, "end": v(-10.39, -27.71) * mm});
            skLineSegment(sketch, "E245.MirrorCS", {"start": v(-35.79, -48.49) * mm, "end": v(-35.79, -53.11) * mm});
            skLineSegment(sketch, "E246.MirrorCS", {"start": v(-40.41, 35.79) * mm, "end": v(-40.41, 40.41) * mm});
            skLineSegment(sketch, "E247.MirrorCS", {"start": v(-27.71, -10.39) * mm, "end": v(-27.71, -15.01) * mm});
            skLineSegment(sketch, "E248.MirrorCS", {"start": v(-40.41, -23.09) * mm, "end": v(-35.79, -23.09) * mm});
            skLineSegment(sketch, "E249.MirrorCS", {"start": v(-35.79, 10.39) * mm, "end": v(-35.79, 15.01) * mm});
            skLineSegment(sketch, "E250.MirrorCS", {"start": v(-40.41, 40.41) * mm, "end": v(-35.79, 40.41) * mm});
            skLineSegment(sketch, "E251", {"start": v(38.1, -35.79) * mm, "end": v(38.1, -31.75) * mm});
            skLineSegment(sketch, "E252", {"start": v(40.41, -50.8) * mm, "end": v(44.5, -50.8) * mm});
            skLineSegment(sketch, "E253", {"start": v(35.79, -50.8) * mm, "end": v(31.75, -50.8) * mm});
            skSolve(sketch);
        }
        {
            var Q0;
            Q0 = qSketchRegion(id + "F0", true);
            extrude(context, id + "F1", {"entities" : qUnion([Q0]), "depth" : 3.17 * mm});
        }
    });
